# Revit family: S-776
name_source: partatom
category: Plumbing Fixtures
revit_build: Autodesk Revit 2015 (Build: 20140606_1530(x64)
units: mm (PartAtom-declared; Revit-internal decimal feet)

## types (6) — shared parameters
B = 72 mm
Description = CHANNEL GRID, SEQUENCE, FOR CHANNELS WIDTH 70
DistExt = 15 mm  [stored 0.0492126 ft]
Grid = INOX AISI304
Manufacturer = Jimten
Material = INOX AISI304
Model = S-776
Type Comments = COMPATIBLE WITH VISIBLE OR THIN FRAMES
URL = http://www.jimten.com

## per-type parameters (varying)
| type | A | N_MatrizHuecos | Reference | Size |
| 70x350mm_SEQUENCE | 340 mm | 3 | 13739 | 350mm x 70mm |
| 70x550mm_SEQUENCE | 540 mm  [stored 1.77165 ft] | 5 | 13759 | 550mm x 70mm |
| 70x650mm_SEQUENCE | 640 mm  [stored 2.09974 ft] | 6 | 13769 | 650mm x 70mm |
| 70x750mm_SEQUENCE | 740 mm | 7 | 13779 | 750mm x 70mm |
| 70x850mm_SEQUENCE | 840 mm | 8 | 13789 | 850mm x 70mm |
| 70x950mm_SEQUENCE | 940 mm | 9 | 13799 | 950mm x 70mm |

note: [stored X ft] marks values corroborated as IEEE doubles in the binary element streams (Revit-internal decimal feet)

## geometry (parser evidence)
native form markers: Blend x3, Sweep x2
no freeform markers — native parametric forms only
